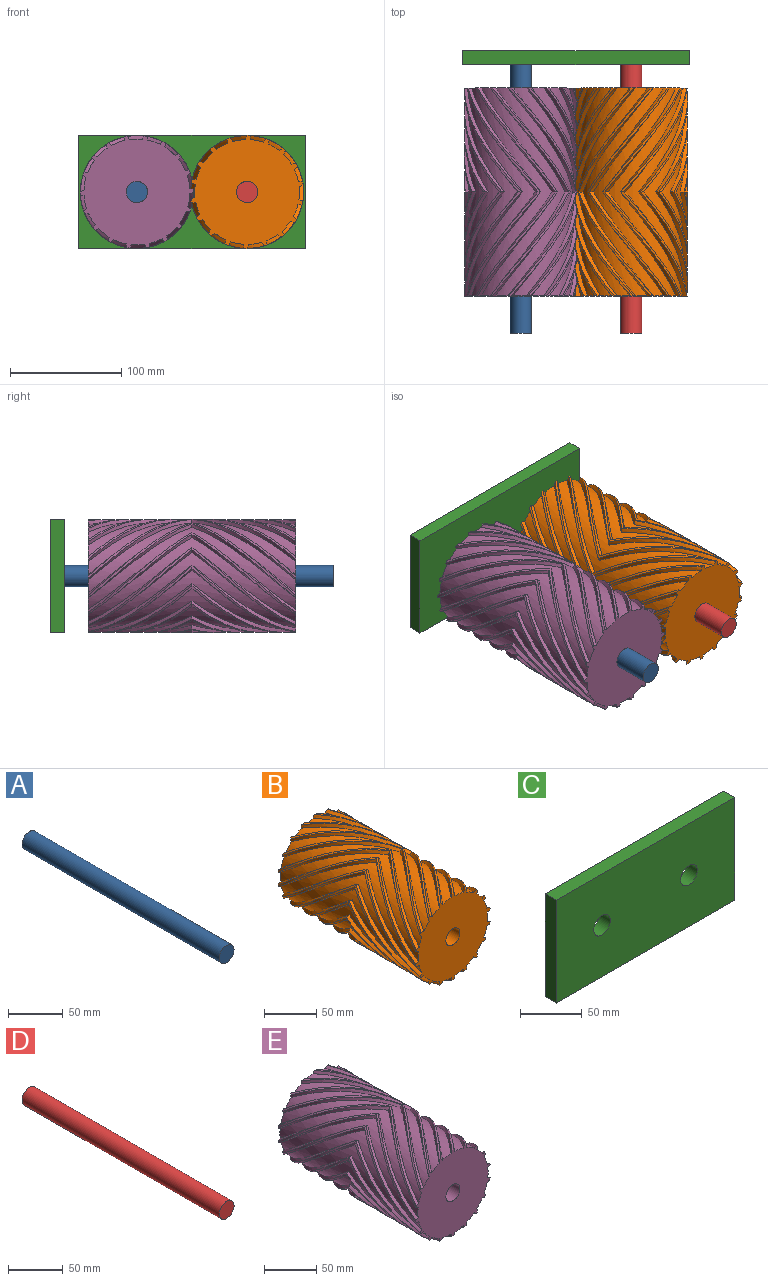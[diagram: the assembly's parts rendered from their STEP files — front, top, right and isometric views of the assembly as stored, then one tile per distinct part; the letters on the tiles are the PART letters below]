
ASSEMBLY  parts=5 mates=4
PART A: 3 faces, bbox 19.1x254x19.1 mm
  f0: cylinder r=9.53mm len=254mm, axis (0,1,0), area 15201.2mm2, adj f1,f2
  f1: plane 19.05x19.05mm, normal (0,-1,0), area 285mm2, adj f0
  f2: plane 19.05x19.05mm, normal (0,1,0), area 285mm2, adj f0
PART B: 129 faces, bbox 102.5x186.9x102.5 mm
  f0: plane 101.65x100.54mm, normal (0,-1,0), area 6946.6mm2, adj f1,f2,f3,f4,f5,f6,f7,f8
  f1: bspline ~93.47x69.89mm, area 471mm2, adj f0,f2,f4,f23
  f2: bspline ~93.47x71.15mm, area 235.9mm2, adj f0,f1,f3,f24
  f3: bspline ~93.47x68.96mm, area 471mm2, adj f0,f2,f16,f25
  f4: cylinder r=47.1mm len=186.94mm, axis (0,1,0), area 2157.7mm2, adj f0,f1,f22,f23,f97,f100
  f5: cylinder r=47.1mm len=186.94mm, axis (0,1,0), area 2157.7mm2, adj f0,f22,f31,f34,f35,f38
  f6: cylinder r=47.1mm len=186.94mm, axis (0,1,0), area 2157.7mm2, adj f0,f22,f37,f40,f41,f44
  f7: cylinder r=47.1mm len=186.94mm, axis (0,1,0), area 2157.7mm2, adj f0,f22,f43,f46,f47,f50
  f8: cylinder r=47.1mm len=186.94mm, axis (0,1,0), area 2157.7mm2, adj f0,f22,f49,f52,f53,f56
  f9: cylinder r=47.1mm len=186.94mm, axis (0,1,0), area 2157.7mm2, adj f0,f22,f55,f58,f59,f62
  f10: cylinder r=47.1mm len=186.94mm, axis (0,1,0), area 2157.7mm2, adj f0,f22,f61,f64,f65,f68
  f11: cylinder r=47.1mm len=186.94mm, axis (0,1,0), area 2157.7mm2, adj f0,f22,f67,f70,f77,f80
  f12: cylinder r=47.1mm len=186.94mm, axis (0,1,0), area 2157.7mm2, adj f0,f22,f73,f76,f89,f92
  f13: cylinder r=47.1mm len=186.94mm, axis (0,1,0), area 2157.7mm2, adj f0,f22,f71,f74,f79,f82
  f14: cylinder r=47.1mm len=186.94mm, axis (0,1,0), area 2157.7mm2, adj f0,f22,f85,f88,f95,f98
  f15: cylinder r=47.1mm len=186.94mm, axis (0,1,0), area 2157.7mm2, adj f0,f22,f83,f86,f91,f94
  f16: cylinder r=47.1mm len=186.94mm, axis (0,1,0), area 2157.7mm2, adj f0,f3,f22,f25,f26,f125
  f17: cylinder r=47.1mm len=186.94mm, axis (0,1,0), area 2157.7mm2, adj f0,f22,f103,f106,f113,f116
  f18: cylinder r=47.1mm len=186.94mm, axis (0,1,0), area 2157.7mm2, adj f0,f22,f29,f32,f109,f112
  f19: cylinder r=47.1mm len=186.94mm, axis (0,1,0), area 2157.7mm2, adj f0,f22,f115,f118,f119,f122
  f20: cylinder r=47.1mm len=186.94mm, axis (0,1,0), area 2157.7mm2, adj f0,f22,f107,f110,f121,f124
  f21: cylinder r=47.1mm len=186.94mm, axis (0,1,0), area 2157.7mm2, adj f0,f22,f28,f101,f104,f127
  f22: plane 101.65x100.54mm, normal (0,1,0), area 6946.6mm2, adj f4,f5,f6,f7,f8,f9,f10,f11
  f23: bspline ~93.47x69.89mm, area 471mm2, adj f1,f4,f22,f24
  f24: bspline ~93.47x71.15mm, area 235.9mm2, adj f2,f22,f23,f25
  f25: bspline ~93.47x68.96mm, area 471mm2, adj f3,f16,f22,f24
  f26: bspline ~93.47x60.41mm, area 471mm2, adj f16,f22,f27,f125
  f27: bspline ~93.47x60.34mm, area 235.9mm2, adj f22,f26,f28,f126
  f28: bspline ~93.47x57.85mm, area 471mm2, adj f21,f22,f27,f127
  f29: bspline ~93.47x53.27mm, area 471mm2, adj f18,f22,f30,f32
  f30: bspline ~93.47x52.25mm, area 235.9mm2, adj f22,f29,f31,f33
  f31: bspline ~93.47x53.27mm, area 471mm2, adj f5,f22,f30,f34
  f32: bspline ~93.47x53.27mm, area 471mm2, adj f0,f18,f29,f33
  f33: bspline ~93.47x52.25mm, area 235.9mm2, adj f0,f30,f32,f34
  f34: bspline ~93.47x53.27mm, area 471mm2, adj f0,f5,f31,f33
  f35: bspline ~93.47x64.39mm, area 471mm2, adj f0,f5,f36,f38
  f36: bspline ~93.47x66.76mm, area 235.9mm2, adj f0,f35,f37,f39
  f37: bspline ~93.47x66.03mm, area 471mm2, adj f0,f6,f36,f40
  f38: bspline ~93.47x64.39mm, area 471mm2, adj f5,f22,f35,f39
  f39: bspline ~93.47x66.76mm, area 235.9mm2, adj f22,f36,f38,f40
  f40: bspline ~93.47x66.03mm, area 471mm2, adj f6,f22,f37,f39
  f41: bspline ~93.47x71.45mm, area 471mm2, adj f0,f6,f42,f44
  f42: bspline ~93.47x73.38mm, area 235.9mm2, adj f0,f41,f43,f45
  f43: bspline ~93.47x71.76mm, area 471mm2, adj f0,f7,f42,f46
  f44: bspline ~93.47x71.45mm, area 471mm2, adj f6,f22,f41,f45
  f45: bspline ~93.47x73.38mm, area 235.9mm2, adj f22,f42,f44,f46
  f46: bspline ~93.47x71.76mm, area 471mm2, adj f7,f22,f43,f45
  f47: bspline ~93.47x69.89mm, area 471mm2, adj f0,f7,f48,f50
  f48: bspline ~93.47x71.15mm, area 235.9mm2, adj f0,f47,f49,f51
  f49: bspline ~93.47x68.96mm, area 471mm2, adj f0,f8,f48,f52
  f50: bspline ~93.47x69.89mm, area 471mm2, adj f7,f22,f47,f51
  f51: bspline ~93.47x71.15mm, area 235.9mm2, adj f22,f48,f50,f52
  f52: bspline ~93.47x68.96mm, area 471mm2, adj f8,f22,f49,f51
  f53: bspline ~93.47x60.41mm, area 471mm2, adj f0,f8,f54,f56
  f54: bspline ~93.47x60.34mm, area 235.9mm2, adj f0,f53,f55,f57
  f55: bspline ~93.47x57.85mm, area 471mm2, adj f0,f9,f54,f58
  f56: bspline ~93.47x60.41mm, area 471mm2, adj f8,f22,f53,f57
  f57: bspline ~93.47x60.34mm, area 235.9mm2, adj f22,f54,f56,f58
  f58: bspline ~93.47x57.85mm, area 471mm2, adj f9,f22,f55,f57
  f59: bspline ~93.47x57.85mm, area 471mm2, adj f0,f9,f60,f62
  f60: bspline ~93.47x60.34mm, area 235.9mm2, adj f0,f59,f61,f63
  f61: bspline ~93.47x60.41mm, area 471mm2, adj f0,f10,f60,f64
  f62: bspline ~93.47x57.85mm, area 471mm2, adj f9,f22,f59,f63
  f63: bspline ~93.47x60.34mm, area 235.9mm2, adj f22,f60,f62,f64
  f64: bspline ~93.47x60.41mm, area 471mm2, adj f10,f22,f61,f63
  f65: bspline ~93.47x68.96mm, area 471mm2, adj f0,f10,f66,f68
  f66: bspline ~93.47x71.15mm, area 235.9mm2, adj f0,f65,f67,f69
  f67: bspline ~93.47x69.89mm, area 471mm2, adj f0,f11,f66,f70
  f68: bspline ~93.47x68.96mm, area 471mm2, adj f10,f22,f65,f69
  f69: bspline ~93.47x71.15mm, area 235.9mm2, adj f22,f66,f68,f70
  f70: bspline ~93.47x69.89mm, area 471mm2, adj f11,f22,f67,f69
  f71: bspline ~93.47x66.03mm, area 471mm2, adj f0,f13,f72,f74
  f72: bspline ~93.47x66.76mm, area 235.9mm2, adj f0,f71,f73,f75
  f73: bspline ~93.47x64.39mm, area 471mm2, adj f0,f12,f72,f76
  f74: bspline ~93.47x66.03mm, area 471mm2, adj f13,f22,f71,f75
  f75: bspline ~93.47x66.76mm, area 235.9mm2, adj f22,f72,f74,f76
  f76: bspline ~93.47x64.39mm, area 471mm2, adj f12,f22,f73,f75
  f77: bspline ~93.47x71.76mm, area 471mm2, adj f0,f11,f78,f80
  f78: bspline ~93.47x73.38mm, area 235.9mm2, adj f0,f77,f79,f81
  f79: bspline ~93.47x71.45mm, area 471mm2, adj f0,f13,f78,f82
  f80: bspline ~93.47x71.76mm, area 471mm2, adj f11,f22,f77,f81
  f81: bspline ~93.47x73.38mm, area 235.9mm2, adj f22,f78,f80,f82
  f82: bspline ~93.47x71.45mm, area 471mm2, adj f13,f22,f79,f81
  f83: bspline ~93.47x64.39mm, area 471mm2, adj f0,f15,f84,f86
  f84: bspline ~93.47x66.76mm, area 235.9mm2, adj f0,f83,f85,f87
  f85: bspline ~93.47x66.03mm, area 471mm2, adj f0,f14,f84,f88
  f86: bspline ~93.47x64.39mm, area 471mm2, adj f15,f22,f83,f87
  f87: bspline ~93.47x66.76mm, area 235.9mm2, adj f22,f84,f86,f88
  f88: bspline ~93.47x66.03mm, area 471mm2, adj f14,f22,f85,f87
  f89: bspline ~93.47x53.27mm, area 471mm2, adj f0,f12,f90,f92
  f90: bspline ~93.47x52.25mm, area 235.9mm2, adj f0,f89,f91,f93
  f91: bspline ~93.47x53.27mm, area 471mm2, adj f0,f15,f90,f94
  f92: bspline ~93.47x53.27mm, area 471mm2, adj f12,f22,f89,f93
  f93: bspline ~93.47x52.25mm, area 235.9mm2, adj f22,f90,f92,f94
  f94: bspline ~93.47x53.27mm, area 471mm2, adj f15,f22,f91,f93
  f95: bspline ~93.47x71.45mm, area 471mm2, adj f0,f14,f96,f98
  f96: bspline ~93.47x73.38mm, area 235.9mm2, adj f0,f95,f97,f99
  f97: bspline ~93.47x71.76mm, area 471mm2, adj f0,f4,f96,f100
  f98: bspline ~93.47x71.45mm, area 471mm2, adj f14,f22,f95,f99
  f99: bspline ~93.47x73.38mm, area 235.9mm2, adj f22,f96,f98,f100
  f100: bspline ~93.47x71.76mm, area 471mm2, adj f4,f22,f97,f99
  f101: bspline ~93.47x57.85mm, area 471mm2, adj f21,f22,f102,f104
  f102: bspline ~93.47x60.34mm, area 235.9mm2, adj f22,f101,f103,f105
  f103: bspline ~93.47x60.41mm, area 471mm2, adj f17,f22,f102,f106
  f104: bspline ~93.47x57.85mm, area 471mm2, adj f0,f21,f101,f105
  f105: bspline ~93.47x60.34mm, area 235.9mm2, adj f0,f102,f104,f106
  f106: bspline ~93.47x60.41mm, area 471mm2, adj f0,f17,f103,f105
  f107: bspline ~93.47x66.03mm, area 471mm2, adj f20,f22,f108,f110
  f108: bspline ~93.47x66.76mm, area 235.9mm2, adj f22,f107,f109,f111
  f109: bspline ~93.47x64.39mm, area 471mm2, adj f18,f22,f108,f112
  f110: bspline ~93.47x66.03mm, area 471mm2, adj f0,f20,f107,f111
  f111: bspline ~93.47x66.76mm, area 235.9mm2, adj f0,f108,f110,f112
  f112: bspline ~93.47x64.39mm, area 471mm2, adj f0,f18,f109,f111
  f113: bspline ~93.47x68.96mm, area 471mm2, adj f17,f22,f114,f116
  f114: bspline ~93.47x71.15mm, area 235.9mm2, adj f22,f113,f115,f117
  f115: bspline ~93.47x69.89mm, area 471mm2, adj f19,f22,f114,f118
  f116: bspline ~93.47x68.96mm, area 471mm2, adj f0,f17,f113,f117
  f117: bspline ~93.47x71.15mm, area 235.9mm2, adj f0,f114,f116,f118
  f118: bspline ~93.47x69.89mm, area 471mm2, adj f0,f19,f115,f117
  f119: bspline ~93.47x71.76mm, area 471mm2, adj f19,f22,f120,f122
  f120: bspline ~93.47x73.38mm, area 235.9mm2, adj f22,f119,f121,f123
  f121: bspline ~93.47x71.45mm, area 471mm2, adj f20,f22,f120,f124
  f122: bspline ~93.47x71.76mm, area 471mm2, adj f0,f19,f119,f123
  f123: bspline ~93.47x73.38mm, area 235.9mm2, adj f0,f120,f122,f124
  f124: bspline ~93.47x71.45mm, area 471mm2, adj f0,f20,f121,f123
  f125: bspline ~93.47x60.41mm, area 471mm2, adj f0,f16,f26,f126
  f126: bspline ~93.47x60.34mm, area 235.9mm2, adj f0,f27,f125,f127
  f127: bspline ~93.47x57.85mm, area 471mm2, adj f0,f21,f28,f126
  f128: cylinder r=9.53mm len=186.94mm, axis (0,1,0), area 11188.1mm2, adj f0,f22
PART C: 8 faces, bbox 203.2x12.7x101.6 mm
  f0: plane 101.6x12.7mm, normal (-1,0,0), area 1290.3mm2, adj f1,f4,f6,f7
  f1: plane 203.2x12.7mm, normal (0,0,-1), area 2580.6mm2, adj f0,f2,f6,f7
  f2: plane 101.6x12.7mm, normal (1,0,0), area 1290.3mm2, adj f1,f4,f6,f7
  f3: cylinder r=9.53mm len=19.05mm, axis (0,-1,0), area 760.1mm2, adj f6,f7
  f4: plane 203.2x12.7mm, normal (0,0,1), area 2580.6mm2, adj f0,f2,f6,f7
  f5: cylinder r=9.53mm len=19.05mm, axis (0,-1,0), area 760.1mm2, adj f6,f7
  f6: plane 203.2x101.6mm, normal (0,1,0), area 20075.1mm2, adj f0,f1,f2,f3,f4,f5
  f7: plane 203.2x101.6mm, normal (0,-1,0), area 20075.1mm2, adj f0,f1,f2,f3,f4,f5
PART D: 3 faces, bbox 19.1x254x19.1 mm
  f0: cylinder r=9.53mm len=254mm, axis (0,1,0), area 15201.2mm2, adj f1,f2
  f1: plane 19.05x19.05mm, normal (0,-1,0), area 285mm2, adj f0
  f2: plane 19.05x19.05mm, normal (0,1,0), area 285mm2, adj f0
PART E: 129 faces, bbox 102.5x186.9x102.5 mm
  f0: plane 101.65x100.54mm, normal (0,-1,0), area 7058.5mm2, adj f1,f2,f3,f4,f5,f6,f7,f8
  f1: bspline ~93.47x69.89mm, area 406.7mm2, adj f0,f2,f4,f23
  f2: bspline ~93.47x71.15mm, area 235.9mm2, adj f0,f1,f3,f24
  f3: bspline ~93.47x68.96mm, area 406.7mm2, adj f0,f2,f16,f25
  f4: cylinder r=47.62mm len=186.94mm, axis (0,1,0), area 2227.2mm2, adj f0,f1,f22,f23,f97,f100
  f5: cylinder r=47.62mm len=186.94mm, axis (0,1,0), area 2227.2mm2, adj f0,f22,f31,f34,f35,f38
  f6: cylinder r=47.62mm len=186.94mm, axis (0,1,0), area 2227.2mm2, adj f0,f22,f37,f40,f41,f44
  f7: cylinder r=47.62mm len=186.94mm, axis (0,1,0), area 2227.2mm2, adj f0,f22,f43,f46,f47,f50
  f8: cylinder r=47.62mm len=186.94mm, axis (0,1,0), area 2227.2mm2, adj f0,f22,f49,f52,f53,f56
  f9: cylinder r=47.62mm len=186.94mm, axis (0,1,0), area 2227.2mm2, adj f0,f22,f55,f58,f59,f62
  f10: cylinder r=47.62mm len=186.94mm, axis (0,1,0), area 2227.2mm2, adj f0,f22,f61,f64,f65,f68
  f11: cylinder r=47.62mm len=186.94mm, axis (0,1,0), area 2227.2mm2, adj f0,f22,f67,f70,f77,f80
  f12: cylinder r=47.62mm len=186.94mm, axis (0,1,0), area 2227.2mm2, adj f0,f22,f73,f76,f89,f92
  f13: cylinder r=47.62mm len=186.94mm, axis (0,1,0), area 2227.2mm2, adj f0,f22,f71,f74,f79,f82
  f14: cylinder r=47.62mm len=186.94mm, axis (0,1,0), area 2227.2mm2, adj f0,f22,f85,f88,f95,f98
  f15: cylinder r=47.62mm len=186.94mm, axis (0,1,0), area 2227.2mm2, adj f0,f22,f83,f86,f91,f94
  f16: cylinder r=47.62mm len=186.94mm, axis (0,1,0), area 2227.2mm2, adj f0,f3,f22,f25,f26,f125
  f17: cylinder r=47.62mm len=186.94mm, axis (0,1,0), area 2227.2mm2, adj f0,f22,f103,f106,f113,f116
  f18: cylinder r=47.62mm len=186.94mm, axis (0,1,0), area 2227.2mm2, adj f0,f22,f29,f32,f109,f112
  f19: cylinder r=47.62mm len=186.94mm, axis (0,1,0), area 2227.2mm2, adj f0,f22,f115,f118,f119,f122
  f20: cylinder r=47.62mm len=186.94mm, axis (0,1,0), area 2227.2mm2, adj f0,f22,f107,f110,f121,f124
  f21: cylinder r=47.62mm len=186.94mm, axis (0,1,0), area 2227.2mm2, adj f0,f22,f28,f101,f104,f127
  f22: plane 101.65x100.54mm, normal (0,1,0), area 7058.5mm2, adj f4,f5,f6,f7,f8,f9,f10,f11
  f23: bspline ~93.47x69.89mm, area 406.7mm2, adj f1,f4,f22,f24
  f24: bspline ~93.47x71.15mm, area 235.9mm2, adj f2,f22,f23,f25
  f25: bspline ~93.47x68.96mm, area 406.7mm2, adj f3,f16,f22,f24
  f26: bspline ~93.47x60.41mm, area 406.7mm2, adj f16,f22,f27,f125
  f27: bspline ~93.47x60.34mm, area 235.9mm2, adj f22,f26,f28,f126
  f28: bspline ~93.47x57.85mm, area 406.7mm2, adj f21,f22,f27,f127
  f29: bspline ~93.47x53.18mm, area 406.7mm2, adj f18,f22,f30,f32
  f30: bspline ~93.47x52.25mm, area 235.9mm2, adj f22,f29,f31,f33
  f31: bspline ~93.47x53.18mm, area 406.7mm2, adj f5,f22,f30,f34
  f32: bspline ~93.47x53.18mm, area 406.7mm2, adj f0,f18,f29,f33
  f33: bspline ~93.47x52.25mm, area 235.9mm2, adj f0,f30,f32,f34
  f34: bspline ~93.47x53.18mm, area 406.7mm2, adj f0,f5,f31,f33
  f35: bspline ~93.47x64.39mm, area 406.7mm2, adj f0,f5,f36,f38
  f36: bspline ~93.47x66.76mm, area 235.9mm2, adj f0,f35,f37,f39
  f37: bspline ~93.47x66.02mm, area 406.7mm2, adj f0,f6,f36,f40
  f38: bspline ~93.47x64.39mm, area 406.7mm2, adj f5,f22,f35,f39
  f39: bspline ~93.47x66.76mm, area 235.9mm2, adj f22,f36,f38,f40
  f40: bspline ~93.47x66.02mm, area 406.7mm2, adj f6,f22,f37,f39
  f41: bspline ~93.47x71.45mm, area 406.7mm2, adj f0,f6,f42,f44
  f42: bspline ~93.47x73.38mm, area 235.9mm2, adj f0,f41,f43,f45
  f43: bspline ~93.47x71.76mm, area 406.7mm2, adj f0,f7,f42,f46
  f44: bspline ~93.47x71.45mm, area 406.7mm2, adj f6,f22,f41,f45
  f45: bspline ~93.47x73.38mm, area 235.9mm2, adj f22,f42,f44,f46
  f46: bspline ~93.47x71.76mm, area 406.7mm2, adj f7,f22,f43,f45
  f47: bspline ~93.47x69.89mm, area 406.7mm2, adj f0,f7,f48,f50
  f48: bspline ~93.47x71.15mm, area 235.9mm2, adj f0,f47,f49,f51
  f49: bspline ~93.47x68.96mm, area 406.7mm2, adj f0,f8,f48,f52
  f50: bspline ~93.47x69.89mm, area 406.7mm2, adj f7,f22,f47,f51
  f51: bspline ~93.47x71.15mm, area 235.9mm2, adj f22,f48,f50,f52
  f52: bspline ~93.47x68.96mm, area 406.7mm2, adj f8,f22,f49,f51
  f53: bspline ~93.47x60.41mm, area 406.7mm2, adj f0,f8,f54,f56
  f54: bspline ~93.47x60.34mm, area 235.9mm2, adj f0,f53,f55,f57
  f55: bspline ~93.47x57.85mm, area 406.7mm2, adj f0,f9,f54,f58
  f56: bspline ~93.47x60.41mm, area 406.7mm2, adj f8,f22,f53,f57
  f57: bspline ~93.47x60.34mm, area 235.9mm2, adj f22,f54,f56,f58
  f58: bspline ~93.47x57.85mm, area 406.7mm2, adj f9,f22,f55,f57
  f59: bspline ~93.47x57.85mm, area 406.7mm2, adj f0,f9,f60,f62
  f60: bspline ~93.47x60.34mm, area 235.9mm2, adj f0,f59,f61,f63
  f61: bspline ~93.47x60.41mm, area 406.7mm2, adj f0,f10,f60,f64
  f62: bspline ~93.47x57.85mm, area 406.7mm2, adj f9,f22,f59,f63
  f63: bspline ~93.47x60.34mm, area 235.9mm2, adj f22,f60,f62,f64
  f64: bspline ~93.47x60.41mm, area 406.7mm2, adj f10,f22,f61,f63
  f65: bspline ~93.47x68.96mm, area 406.7mm2, adj f0,f10,f66,f68
  f66: bspline ~93.47x71.15mm, area 235.9mm2, adj f0,f65,f67,f69
  f67: bspline ~93.47x69.89mm, area 406.7mm2, adj f0,f11,f66,f70
  f68: bspline ~93.47x68.96mm, area 406.7mm2, adj f10,f22,f65,f69
  f69: bspline ~93.47x71.15mm, area 235.9mm2, adj f22,f66,f68,f70
  f70: bspline ~93.47x69.89mm, area 406.7mm2, adj f11,f22,f67,f69
  f71: bspline ~93.47x66.02mm, area 406.7mm2, adj f0,f13,f72,f74
  f72: bspline ~93.47x66.76mm, area 235.9mm2, adj f0,f71,f73,f75
  f73: bspline ~93.47x64.39mm, area 406.7mm2, adj f0,f12,f72,f76
  f74: bspline ~93.47x66.02mm, area 406.7mm2, adj f13,f22,f71,f75
  f75: bspline ~93.47x66.76mm, area 235.9mm2, adj f22,f72,f74,f76
  f76: bspline ~93.47x64.39mm, area 406.7mm2, adj f12,f22,f73,f75
  f77: bspline ~93.47x71.76mm, area 406.7mm2, adj f0,f11,f78,f80
  f78: bspline ~93.47x73.38mm, area 235.9mm2, adj f0,f77,f79,f81
  f79: bspline ~93.47x71.45mm, area 406.7mm2, adj f0,f13,f78,f82
  f80: bspline ~93.47x71.76mm, area 406.7mm2, adj f11,f22,f77,f81
  f81: bspline ~93.47x73.38mm, area 235.9mm2, adj f22,f78,f80,f82
  f82: bspline ~93.47x71.45mm, area 406.7mm2, adj f13,f22,f79,f81
  f83: bspline ~93.47x64.39mm, area 406.7mm2, adj f0,f15,f84,f86
  f84: bspline ~93.47x66.76mm, area 235.9mm2, adj f0,f83,f85,f87
  f85: bspline ~93.47x66.02mm, area 406.7mm2, adj f0,f14,f84,f88
  f86: bspline ~93.47x64.39mm, area 406.7mm2, adj f15,f22,f83,f87
  f87: bspline ~93.47x66.76mm, area 235.9mm2, adj f22,f84,f86,f88
  f88: bspline ~93.47x66.02mm, area 406.7mm2, adj f14,f22,f85,f87
  f89: bspline ~93.47x53.18mm, area 406.7mm2, adj f0,f12,f90,f92
  f90: bspline ~93.47x52.25mm, area 235.9mm2, adj f0,f89,f91,f93
  f91: bspline ~93.47x53.18mm, area 406.7mm2, adj f0,f15,f90,f94
  f92: bspline ~93.47x53.18mm, area 406.7mm2, adj f12,f22,f89,f93
  f93: bspline ~93.47x52.25mm, area 235.9mm2, adj f22,f90,f92,f94
  f94: bspline ~93.47x53.18mm, area 406.7mm2, adj f15,f22,f91,f93
  f95: bspline ~93.47x71.45mm, area 406.7mm2, adj f0,f14,f96,f98
  f96: bspline ~93.47x73.38mm, area 235.9mm2, adj f0,f95,f97,f99
  f97: bspline ~93.47x71.76mm, area 406.7mm2, adj f0,f4,f96,f100
  f98: bspline ~93.47x71.45mm, area 406.7mm2, adj f14,f22,f95,f99
  f99: bspline ~93.47x73.38mm, area 235.9mm2, adj f22,f96,f98,f100
  f100: bspline ~93.47x71.76mm, area 406.7mm2, adj f4,f22,f97,f99
  f101: bspline ~93.47x57.85mm, area 406.7mm2, adj f21,f22,f102,f104
  f102: bspline ~93.47x60.34mm, area 235.9mm2, adj f22,f101,f103,f105
  f103: bspline ~93.47x60.41mm, area 406.7mm2, adj f17,f22,f102,f106
  f104: bspline ~93.47x57.85mm, area 406.7mm2, adj f0,f21,f101,f105
  f105: bspline ~93.47x60.34mm, area 235.9mm2, adj f0,f102,f104,f106
  f106: bspline ~93.47x60.41mm, area 406.7mm2, adj f0,f17,f103,f105
  f107: bspline ~93.47x66.02mm, area 406.7mm2, adj f20,f22,f108,f110
  f108: bspline ~93.47x66.76mm, area 235.9mm2, adj f22,f107,f109,f111
  f109: bspline ~93.47x64.39mm, area 406.7mm2, adj f18,f22,f108,f112
  f110: bspline ~93.47x66.02mm, area 406.7mm2, adj f0,f20,f107,f111
  f111: bspline ~93.47x66.76mm, area 235.9mm2, adj f0,f108,f110,f112
  f112: bspline ~93.47x64.39mm, area 406.7mm2, adj f0,f18,f109,f111
  f113: bspline ~93.47x68.96mm, area 406.7mm2, adj f17,f22,f114,f116
  f114: bspline ~93.47x71.15mm, area 235.9mm2, adj f22,f113,f115,f117
  f115: bspline ~93.47x69.89mm, area 406.7mm2, adj f19,f22,f114,f118
  f116: bspline ~93.47x68.96mm, area 406.7mm2, adj f0,f17,f113,f117
  f117: bspline ~93.47x71.15mm, area 235.9mm2, adj f0,f114,f116,f118
  f118: bspline ~93.47x69.89mm, area 406.7mm2, adj f0,f19,f115,f117
  f119: bspline ~93.47x71.76mm, area 406.7mm2, adj f19,f22,f120,f122
  f120: bspline ~93.47x73.38mm, area 235.9mm2, adj f22,f119,f121,f123
  f121: bspline ~93.47x71.45mm, area 406.7mm2, adj f20,f22,f120,f124
  f122: bspline ~93.47x71.76mm, area 406.7mm2, adj f0,f19,f119,f123
  f123: bspline ~93.47x73.38mm, area 235.9mm2, adj f0,f120,f122,f124
  f124: bspline ~93.47x71.45mm, area 406.7mm2, adj f0,f20,f121,f123
  f125: bspline ~93.47x60.41mm, area 406.7mm2, adj f0,f16,f26,f126
  f126: bspline ~93.47x60.34mm, area 235.9mm2, adj f0,f27,f125,f127
  f127: bspline ~93.47x57.85mm, area 406.7mm2, adj f0,f21,f28,f126
  f128: cylinder r=9.53mm len=186.94mm, axis (0,1,0), area 11188.1mm2, adj f0,f22
PLACE A t=(22.2,238.7,174.31)mm
PLACE B rot(axis=(-0.33,0,0.94),180deg) t=(71.73,111.7,174.31)mm
PLACE C t=(22.2,226,174.31)mm fixed
PLACE D t=(22.2,238.7,174.31)mm
PLACE E rot(axis=(0,-1,0),51.2deg) t=(-27.33,111.7,174.31)mm
MATE revolute B.f4 <-> D.f0  axis (0,-1,0) through (71.73,111.7,174.31)mm
MATE fastened A.f0 <-> C.f3  axis (0,1,0) through (-27.33,238.7,174.31)mm
MATE revolute E.f4 <-> A.f0  axis (0,1,0) through (-27.33,111.7,174.31)mm
MATE fastened D.f0 <-> C.f5  axis (0,1,0) through (71.73,238.7,174.31)mm
